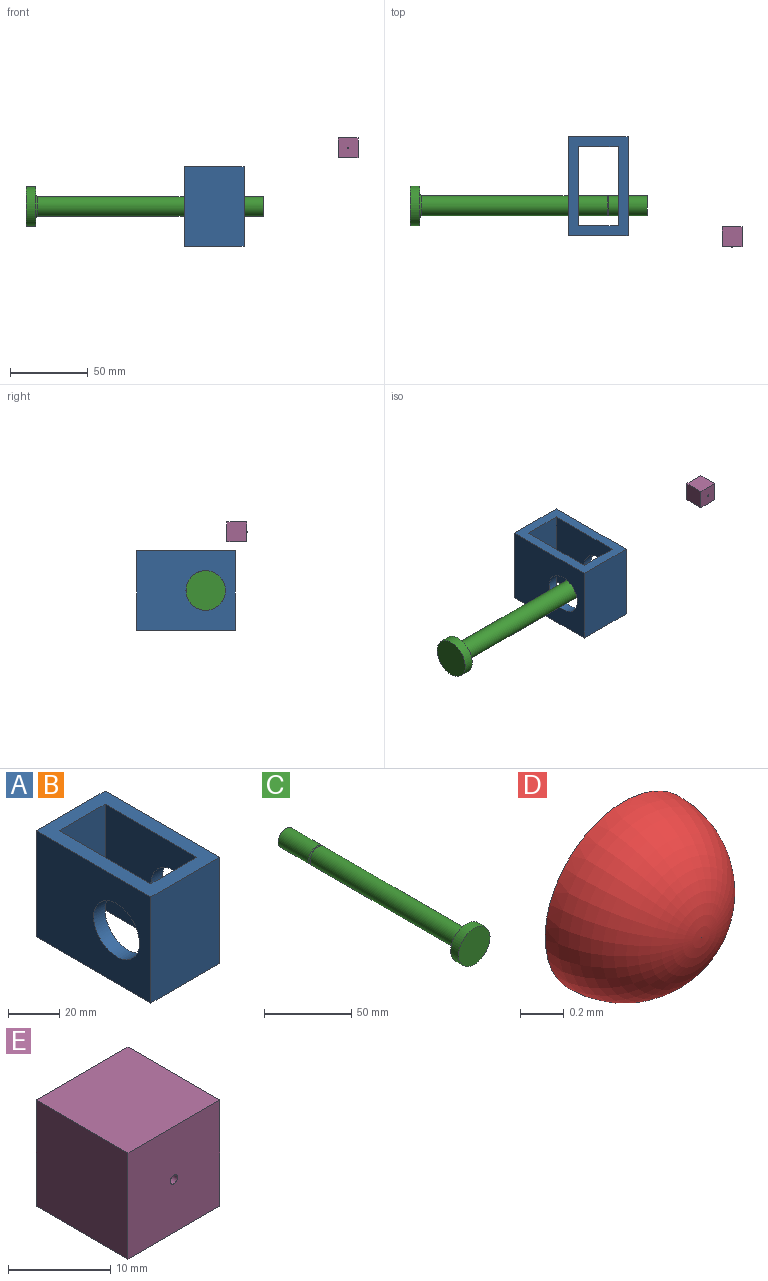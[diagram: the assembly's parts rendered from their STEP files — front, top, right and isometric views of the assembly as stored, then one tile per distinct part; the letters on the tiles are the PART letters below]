
ASSEMBLY  parts=5 mates=2
PART A: 12 faces, bbox 38.1x63.5x50.8 mm
  f0: plane 63.5x38.1mm, normal (0,0,-1), area 1129mm2, adj f3,f5,f6,f7,f8,f9,f10,f11
  f1: plane 63.5x38.1mm, normal (0,0,1), area 1129mm2, adj f3,f5,f6,f7,f8,f9,f10,f11
  f2: cylinder r=12.7mm len=25.4mm, axis (-1,0,0), area 506.7mm2, adj f6,f9
  f3: plane 50.8x38.1mm, normal (0,1,0), area 1935.5mm2, adj f0,f1,f6,f7
  f4: cylinder r=12.7mm len=25.4mm, axis (-1,0,0), area 506.7mm2, adj f7,f11
  f5: plane 50.8x38.1mm, normal (0,-1,0), area 1935.5mm2, adj f0,f1,f6,f7
  f6: plane 63.5x50.8mm, normal (1,0,0), area 2719.1mm2, adj f0,f1,f2,f3,f5
  f7: plane 63.5x50.8mm, normal (-1,0,0), area 2719.1mm2, adj f0,f1,f3,f4,f5
  f8: plane 50.8x25.4mm, normal (0,1,0), area 1290.3mm2, adj f0,f1,f9,f11
  f9: plane 50.8x50.8mm, normal (-1,0,0), area 2073.9mm2, adj f0,f1,f2,f8,f10
  f10: plane 50.8x25.4mm, normal (0,-1,0), area 1290.3mm2, adj f0,f1,f9,f11
  f11: plane 50.8x50.8mm, normal (1,0,0), area 2073.9mm2, adj f0,f1,f4,f8,f10
PART B: same geometry as A
PART C: 8 faces, bbox 25.4x152.4x25.4 mm
  f0: plane 12.7x12.7mm, normal (0,1,0), area 126.7mm2, adj f1
  f1: cylinder r=6.35mm len=24.89mm, axis (0,-1,0), area 993.1mm2, adj f0,f2
  f2: torus R=6.35mm, axis (0,-1,0), area 60.4mm2, adj f1,f3
  f3: cylinder r=6.35mm len=118.87mm, axis (0,-1,0), area 4742.8mm2, adj f2,f7
  f4: plane 25.4x25.4mm, normal (0,1,0), area 324.3mm2, adj f5,f7
  f5: cylinder r=12.7mm len=25.4mm, axis (0,-1,0), area 506.7mm2, adj f4,f6
  f6: plane 25.4x25.4mm, normal (0,-1,0), area 506.7mm2, adj f5
  f7: torus R=7.62mm, axis (0,-1,0), area 85.4mm2, adj f3,f4
PART D: 2 faces, bbox 1x0.5x1 mm
  f0: plane 1.02x1.02mm, normal (0,1,0), area 0.8mm2, adj f1
  f1: torus R=0mm, axis (0,1,0), area 1.6mm2, adj f0
PART E: 7 faces, bbox 12.7x12.7x12.7 mm
  f0: plane 12.7x12.7mm, normal (-1,0,0), area 161.3mm2, adj f1,f4,f5,f6
  f1: plane 12.7x12.7mm, normal (0,0,1), area 161.3mm2, adj f0,f2,f5,f6
  f2: plane 12.7x12.7mm, normal (1,0,0), area 161.3mm2, adj f1,f4,f5,f6
  f3: cylinder r=0.51mm len=12.7mm, axis (0,-1,0), area 40.5mm2, adj f5,f6
  f4: plane 12.7x12.7mm, normal (0,0,-1), area 161.3mm2, adj f0,f2,f5,f6
  f5: plane 12.7x12.7mm, normal (0,1,0), area 160.5mm2, adj f0,f1,f2,f3,f4
  f6: plane 12.7x12.7mm, normal (0,-1,0), area 160.5mm2, adj f0,f1,f2,f3,f4
PLACE A t=(-10.11,4.32,-1.27)mm
PLACE B t=(-10.11,4.32,-1.27)mm
PLACE C rot(axis=(-0.58,-0.58,-0.58),120deg) t=(-68.85,-8.38,-1.27)mm
PLACE D t=(94.82,-34.65,36.39)mm
PLACE E t=(94.82,-34.65,36.39)mm
MATE fastened D.f1 <-> E.f3  axis (0,1,0) through (94.82,-34.65,36.39)mm
MATE cylindrical C.f1 <-> B.f2  axis (-1,0,0) through (27.99,-8.38,-1.27)mm
